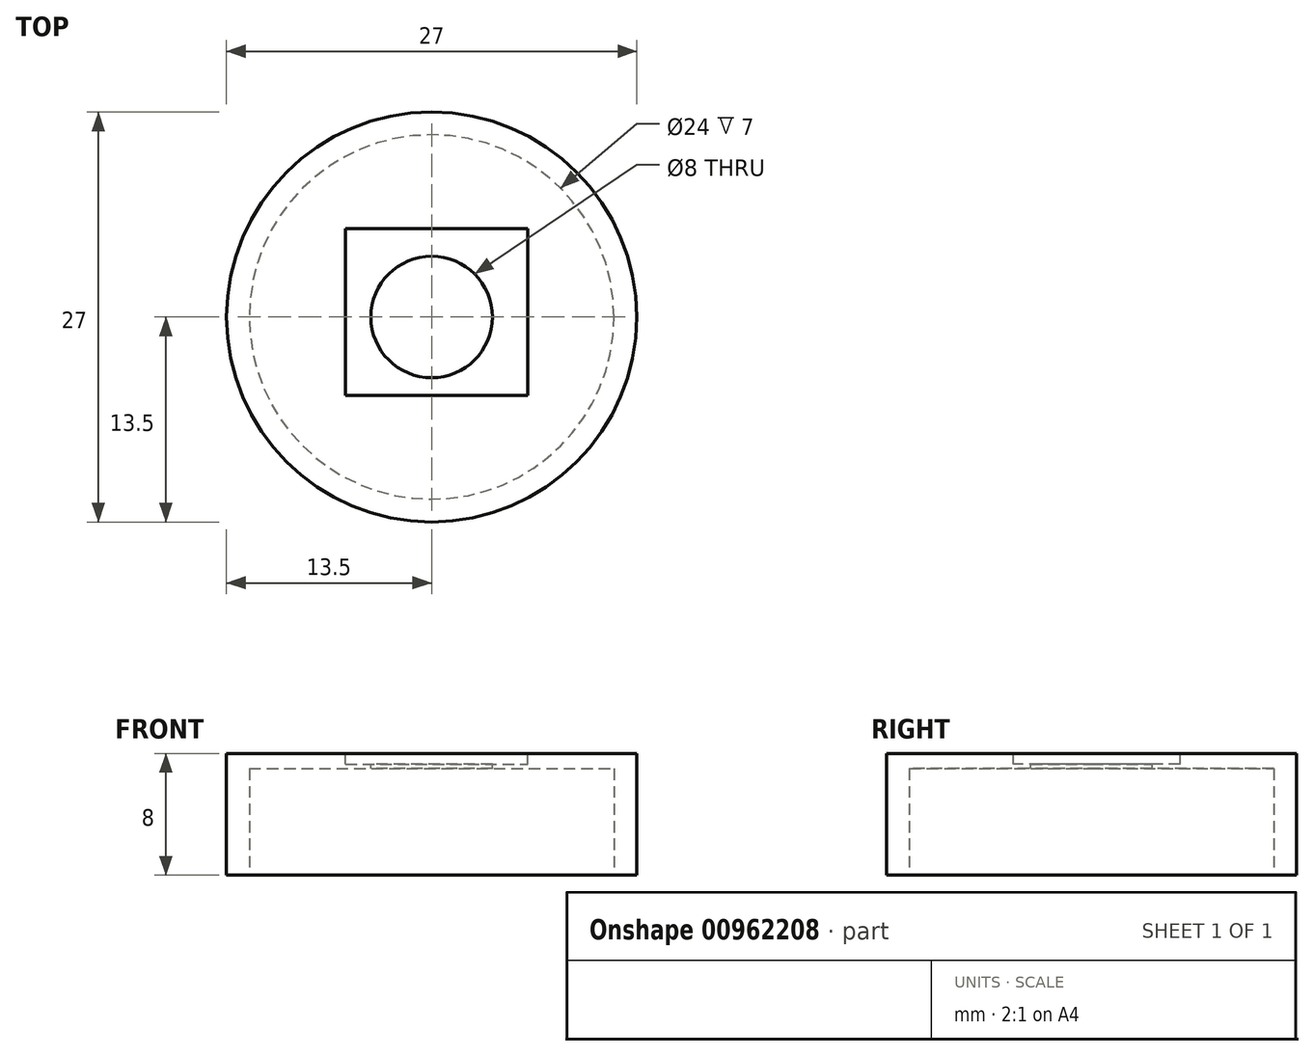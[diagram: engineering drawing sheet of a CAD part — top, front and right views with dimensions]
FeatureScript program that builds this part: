
annotation { "Feature Type Name" : "Feature", "Feature Type Description" : "" }
export const myFeature = defineFeature(function(context is Context, id is Id, definition is map)
    precondition{}
    {
        {
            var Q0;
            Q0=qCreatedBy(makeId("Top.planeOp"),FACE);
            var sketch = newSketch(context, id + "F0", { "sketchPlane" : qUnion([Q0])});
            skCircle(sketch, "E0", {"center": v(0, 0) * mm, "radius": 13.5 * mm});
            skSolve(sketch);
        }
        {
            var Q0;
            Q0=qSketchRegion(id+"F0",true);
            extrude(context, id + "F1", {"entities" : qUnion([Q0]), "depth" : 8 * mm, "offsetDistance" : 25 * mm});
        }
        {
            var Q0;
            Q0=makeQuery(id+"F1.opExtrude","CAP_FACE",FACE,{"disambiguationData":[OSD([sQuery(id+"F0.wireOp",EDGE,"E0")])],"isStart":true});
            var sketch = newSketch(context, id + "F2", { "sketchPlane" : qUnion([Q0])});
            skCircle(sketch, "E1", {"center": v(0, 0) * mm, "radius": 12 * mm});
            skSolve(sketch);
        }
        {
            var Q0;
            Q0=makeQuery(id+"F2.imprint","IMPRINT",FACE,{"disambiguationData":[TD([[makeQuery(id+"F2.imprint","IMPRINT",EDGE,{"derivedFrom":sQuery(id+"F2.wireOp",EDGE,"E1")}),1.0]])]});
            extrude(context, id + "F3", {"entities" : qUnion([Q0]), "operationType" : NewBodyOperationType.REMOVE, "oppositeDirection" : true, "depth" : 7 * mm, "offsetDistance" : 25 * mm});
        }
        {
            var Q0;
            Q0=makeQuery(id+"F1.opExtrude","CAP_FACE",FACE,{"disambiguationData":[OSD([sQuery(id+"F0.wireOp",EDGE,"E0")])],"isStart":false});
            var sketch = newSketch(context, id + "F4", { "sketchPlane" : qUnion([Q0])});
            skLineSegment(sketch, "E2.bottom", {"start": v(-5.67, 5.84) * mm, "end": v(6.33, 5.84) * mm});
            skLineSegment(sketch, "E2.top", {"start": v(-5.67, -5.16) * mm, "end": v(6.33, -5.16) * mm});
            skLineSegment(sketch, "E2.left", {"start": v(-5.67, 5.84) * mm, "end": v(-5.67, -5.16) * mm});
            skLineSegment(sketch, "E2.right", {"start": v(6.33, 5.84) * mm, "end": v(6.33, -5.16) * mm});
            skSolve(sketch);
        }
        {
            var Q0;
            Q0=makeQuery(id+"F4.imprint","IMPRINT",FACE,{"disambiguationData":[TD([[makeQuery(id+"F4.imprint","IMPRINT",EDGE,{"derivedFrom":sQuery(id+"F4.wireOp",EDGE,"E2.bottom")}),-1.0]])]});
            extrude(context, id + "F5", {"entities" : qUnion([Q0]), "operationType" : NewBodyOperationType.REMOVE, "oppositeDirection" : true, "depth" : 0.7 * mm, "offsetDistance" : 25 * mm});
        }
        {
            var Q0;
            Q0=makeQuery(id+"F5.boolean.opBoolean","COPY",FACE,{"derivedFrom":makeQuery(id+"F5.opExtrude","CAP_FACE",FACE,{"disambiguationData":[OSD([sQuery(id+"F4.wireOp",EDGE,"E2.bottom"),sQuery(id+"F4.wireOp",EDGE,"E2.top"),sQuery(id+"F4.wireOp",EDGE,"E2.left"),sQuery(id+"F4.wireOp",EDGE,"E2.right")])],"isStart":false})});
            var sketch = newSketch(context, id + "F6", { "sketchPlane" : qUnion([Q0])});
            skCircle(sketch, "E3", {"center": v(0, 0) * mm, "radius": 4 * mm});
            skSolve(sketch);
        }
        {
            var Q0;
            Q0=makeQuery(id+"F6.imprint","IMPRINT",FACE,{"disambiguationData":[TD([[makeQuery(id+"F6.imprint","IMPRINT",EDGE,{"derivedFrom":sQuery(id+"F6.wireOp",EDGE,"E3")}),1.0]])]});
            extrude(context, id + "F7", {"entities" : qUnion([Q0]), "operationType" : NewBodyOperationType.REMOVE, "oppositeDirection" : true, "depth" : 0.3 * mm, "offsetDistance" : 25 * mm});
        }
    });
